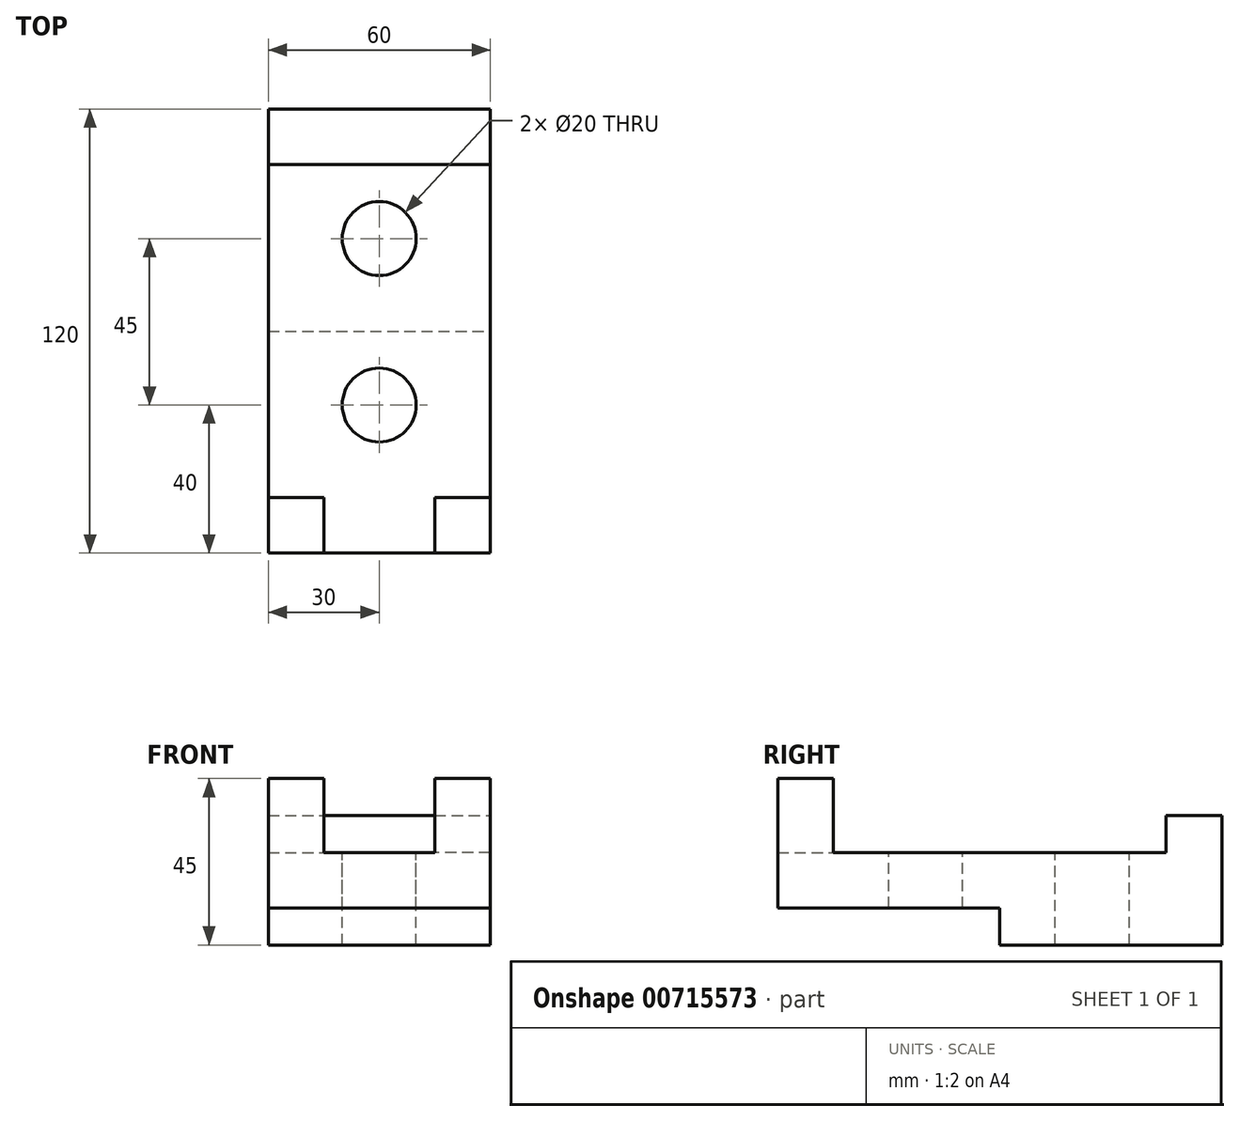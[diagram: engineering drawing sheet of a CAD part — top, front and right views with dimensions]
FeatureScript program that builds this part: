
annotation { "Feature Type Name" : "Feature", "Feature Type Description" : "" }
export const myFeature = defineFeature(function(context is Context, id is Id, definition is map)
    precondition{}
    {
        {
            var Q0;
            Q0=qCreatedBy(makeId("Top.planeOp"),FACE);
            var sketch = newSketch(context, id + "F0", { "sketchPlane" : qUnion([Q0])});
            skLineSegment(sketch, "E0.bottom", {"start": v(30, 60) * mm, "end": v(-30, 60) * mm});
            skLineSegment(sketch, "E0.top", {"start": v(30, -60) * mm, "end": v(-30, -60) * mm});
            skLineSegment(sketch, "E0.left", {"start": v(30, 60) * mm, "end": v(30, -60) * mm});
            skLineSegment(sketch, "E0.right", {"start": v(-30, 60) * mm, "end": v(-30, -60) * mm});
            skPoint(sketch, "E0.middle", {"position": v(0, 0) * mm});
            skSolve(sketch);
        }
        {
            var Q0;
            Q0=makeQuery(id+"F0.imprint","IMPRINT",FACE,{"disambiguationData":[TD([[makeQuery(id+"F0.imprint","IMPRINT",EDGE,{"derivedFrom":sQuery(id+"F0.wireOp",EDGE,"E0.bottom")}),1.0]])]});
            extrude(context, id + "F1", {"entities" : qUnion([Q0]), "depth" : 15 * mm, "offsetDistance" : 25 * mm});
        }
        {
            var Q0;
            Q0=makeQuery(id+"F1.opExtrude","CAP_FACE",FACE,{"disambiguationData":[OSD([sQuery(id+"F0.wireOp",EDGE,"E0.bottom"),sQuery(id+"F0.wireOp",EDGE,"E0.top"),sQuery(id+"F0.wireOp",EDGE,"E0.left"),sQuery(id+"F0.wireOp",EDGE,"E0.right")])],"isStart":false});
            var sketch = newSketch(context, id + "F2", { "sketchPlane" : qUnion([Q0])});
            skLineSegment(sketch, "E1.bottom", {"start": v(-30, 60) * mm, "end": v(30, 60) * mm});
            skLineSegment(sketch, "E1.top", {"start": v(-30, 45) * mm, "end": v(30, 45) * mm});
            skLineSegment(sketch, "E1.left", {"start": v(-30, 60) * mm, "end": v(-30, 45) * mm});
            skLineSegment(sketch, "E1.right", {"start": v(30, 60) * mm, "end": v(30, 45) * mm});
            skSolve(sketch);
        }
        {
            var Q0;
            Q0=makeQuery(id+"F2.imprint","IMPRINT",FACE,{"disambiguationData":[TD([[makeQuery(id+"F2.imprint","IMPRINT",EDGE,{"derivedFrom":sQuery(id+"F2.wireOp",EDGE,"E1.bottom")}),1.0]])]});
            extrude(context, id + "F3", {"entities" : qUnion([Q0]), "operationType" : NewBodyOperationType.ADD, "depth" : 10 * mm, "offsetDistance" : 25 * mm});
        }
        {
            var Q0;
            Q0=makeQuery(id+"F1.opExtrude","CAP_FACE",FACE,{"disambiguationData":[OSD([sQuery(id+"F0.wireOp",EDGE,"E0.bottom"),sQuery(id+"F0.wireOp",EDGE,"E0.top"),sQuery(id+"F0.wireOp",EDGE,"E0.left"),sQuery(id+"F0.wireOp",EDGE,"E0.right")])],"isStart":false});
            var sketch = newSketch(context, id + "F4", { "sketchPlane" : qUnion([Q0])});
            skLineSegment(sketch, "E2.bottom", {"start": v(-30, -60) * mm, "end": v(-15, -60) * mm});
            skLineSegment(sketch, "E2.top", {"start": v(-30, -45) * mm, "end": v(-15, -45) * mm});
            skLineSegment(sketch, "E2.left", {"start": v(-30, -60) * mm, "end": v(-30, -45) * mm});
            skLineSegment(sketch, "E2.right", {"start": v(-15, -60) * mm, "end": v(-15, -45) * mm});
            skLineSegment(sketch, "E3.bottom", {"start": v(30, -60) * mm, "end": v(15, -60) * mm});
            skLineSegment(sketch, "E3.top", {"start": v(30, -45) * mm, "end": v(15, -45) * mm});
            skLineSegment(sketch, "E3.left", {"start": v(30, -60) * mm, "end": v(30, -45) * mm});
            skLineSegment(sketch, "E3.right", {"start": v(15, -60) * mm, "end": v(15, -45) * mm});
            skSolve(sketch);
        }
        {
            var Q0;
            Q0=makeQuery(id+"F4.imprint","IMPRINT",FACE,{"disambiguationData":[TD([[makeQuery(id+"F4.imprint","IMPRINT",EDGE,{"derivedFrom":sQuery(id+"F4.wireOp",EDGE,"E2.bottom")}),-1.0]])]});
            var Q1;
            Q1=makeQuery(id+"F4.imprint","IMPRINT",FACE,{"disambiguationData":[TD([[makeQuery(id+"F4.imprint","IMPRINT",EDGE,{"derivedFrom":sQuery(id+"F4.wireOp",EDGE,"E3.bottom")}),-1.0]])]});
            extrude(context, id + "F5", {"entities" : qUnion([Q0, Q1]), "operationType" : NewBodyOperationType.ADD, "depth" : 10 * mm, "offsetDistance" : 25 * mm});
        }
        {
            var Q0;
            Q0=makeQuery(id+"F1.opExtrude","CAP_FACE",FACE,{"disambiguationData":[OSD([sQuery(id+"F0.wireOp",EDGE,"E0.bottom"),sQuery(id+"F0.wireOp",EDGE,"E0.top"),sQuery(id+"F0.wireOp",EDGE,"E0.left"),sQuery(id+"F0.wireOp",EDGE,"E0.right")])],"isStart":true});
            var sketch = newSketch(context, id + "F6", { "sketchPlane" : qUnion([Q0])});
            skLineSegment(sketch, "E4.bottom", {"start": v(-30, -60) * mm, "end": v(30, -60) * mm});
            skLineSegment(sketch, "E4.top", {"start": v(-30, 0) * mm, "end": v(30, 0) * mm});
            skLineSegment(sketch, "E4.left", {"start": v(-30, -60) * mm, "end": v(-30, 0) * mm});
            skLineSegment(sketch, "E4.right", {"start": v(30, -60) * mm, "end": v(30, 0) * mm});
            skSolve(sketch);
        }
        {
            var Q0;
            Q0=makeQuery(id+"F6.imprint","IMPRINT",FACE,{"disambiguationData":[TD([[makeQuery(id+"F6.imprint","IMPRINT",EDGE,{"derivedFrom":sQuery(id+"F6.wireOp",EDGE,"E4.bottom")}),-1.0]])]});
            extrude(context, id + "F7", {"entities" : qUnion([Q0]), "operationType" : NewBodyOperationType.ADD, "depth" : 10 * mm, "offsetDistance" : 25 * mm});
        }
        {
            var Q0;
            Q0=makeQuery(id+"F5.opExtrude","CAP_FACE",FACE,{"disambiguationData":[OSD([sQuery(id+"F4.wireOp",EDGE,"E2.bottom"),sQuery(id+"F4.wireOp",EDGE,"E2.top"),sQuery(id+"F4.wireOp",EDGE,"E2.left"),sQuery(id+"F4.wireOp",EDGE,"E2.right")])],"isStart":false});
            var Q1;
            Q1=makeQuery(id+"F5.opExtrude","CAP_FACE",FACE,{"disambiguationData":[OSD([sQuery(id+"F4.wireOp",EDGE,"E3.bottom"),sQuery(id+"F4.wireOp",EDGE,"E3.top"),sQuery(id+"F4.wireOp",EDGE,"E3.left"),sQuery(id+"F4.wireOp",EDGE,"E3.right")])],"isStart":false});
            extrude(context, id + "F8", {"entities" : qUnion([Q0, Q1]), "operationType" : NewBodyOperationType.ADD, "depth" : 10 * mm, "offsetDistance" : 25 * mm});
        }
        {
            var Q0;
            Q0=makeQuery(id+"F1.opExtrude","CAP_FACE",FACE,{"disambiguationData":[OSD([sQuery(id+"F0.wireOp",EDGE,"E0.bottom"),sQuery(id+"F0.wireOp",EDGE,"E0.top"),sQuery(id+"F0.wireOp",EDGE,"E0.left"),sQuery(id+"F0.wireOp",EDGE,"E0.right")])],"isStart":false});
            var sketch = newSketch(context, id + "F9", { "sketchPlane" : qUnion([Q0])});
            skLineSegment(sketch, "E5", {"start": v(0, 45) * mm, "end": v(0, 25) * mm});
            skLineSegment(sketch, "E6", {"start": v(0, 25) * mm, "end": v(0, -20) * mm});
            skCircle(sketch, "E7", {"center": v(0, 25) * mm, "radius": 10 * mm});
            skCircle(sketch, "E8", {"center": v(0, -20) * mm, "radius": 10 * mm});
            skSolve(sketch);
        }
        {
            var Q0;
            {var subQ0=sQuery(id+"F9.wireOp",EDGE,"E6");var subQ1=sQuery(id+"F9.wireOp",EDGE,"E5");var subQ2=makeQuery(id+"F9.imprint","INTERSECT",VERTEX,{"derivedFrom":[subQ1,subQ0]});Q0=makeQuery(id+"F9.imprint","IMPRINT",FACE,{"disambiguationData":[TD([[makeQuery(id+"F9.imprint","IMPRINT",EDGE,{"disambiguationData":[TD([[subQ2,1.0]])],"derivedFrom":subQ1}),1.0]])]});}
            var Q1;
            {var subQ0=sQuery(id+"F9.wireOp",EDGE,"E6");var subQ1=sQuery(id+"F9.wireOp",EDGE,"E5");var subQ2=makeQuery(id+"F9.imprint","INTERSECT",VERTEX,{"derivedFrom":[subQ1,subQ0]});Q1=makeQuery(id+"F9.imprint","IMPRINT",FACE,{"disambiguationData":[TD([[makeQuery(id+"F9.imprint","IMPRINT",EDGE,{"disambiguationData":[TD([[subQ2,1.0]])],"derivedFrom":subQ1}),-1.0]])]});}
            var Q2;
            Q2=makeQuery(id+"F9.imprint","IMPRINT",FACE,{"disambiguationData":[TD([[makeQuery(id+"F9.imprint","IMPRINT",EDGE,{"derivedFrom":sQuery(id+"F9.wireOp",EDGE,"E8")}),1.0]])]});
            extrude(context, id + "F10", {"entities" : qUnion([Q0, Q1, Q2]), "operationType" : NewBodyOperationType.REMOVE, "oppositeDirection" : true, "depth" : 52.8 * mm, "offsetDistance" : 25 * mm});
        }
    });
